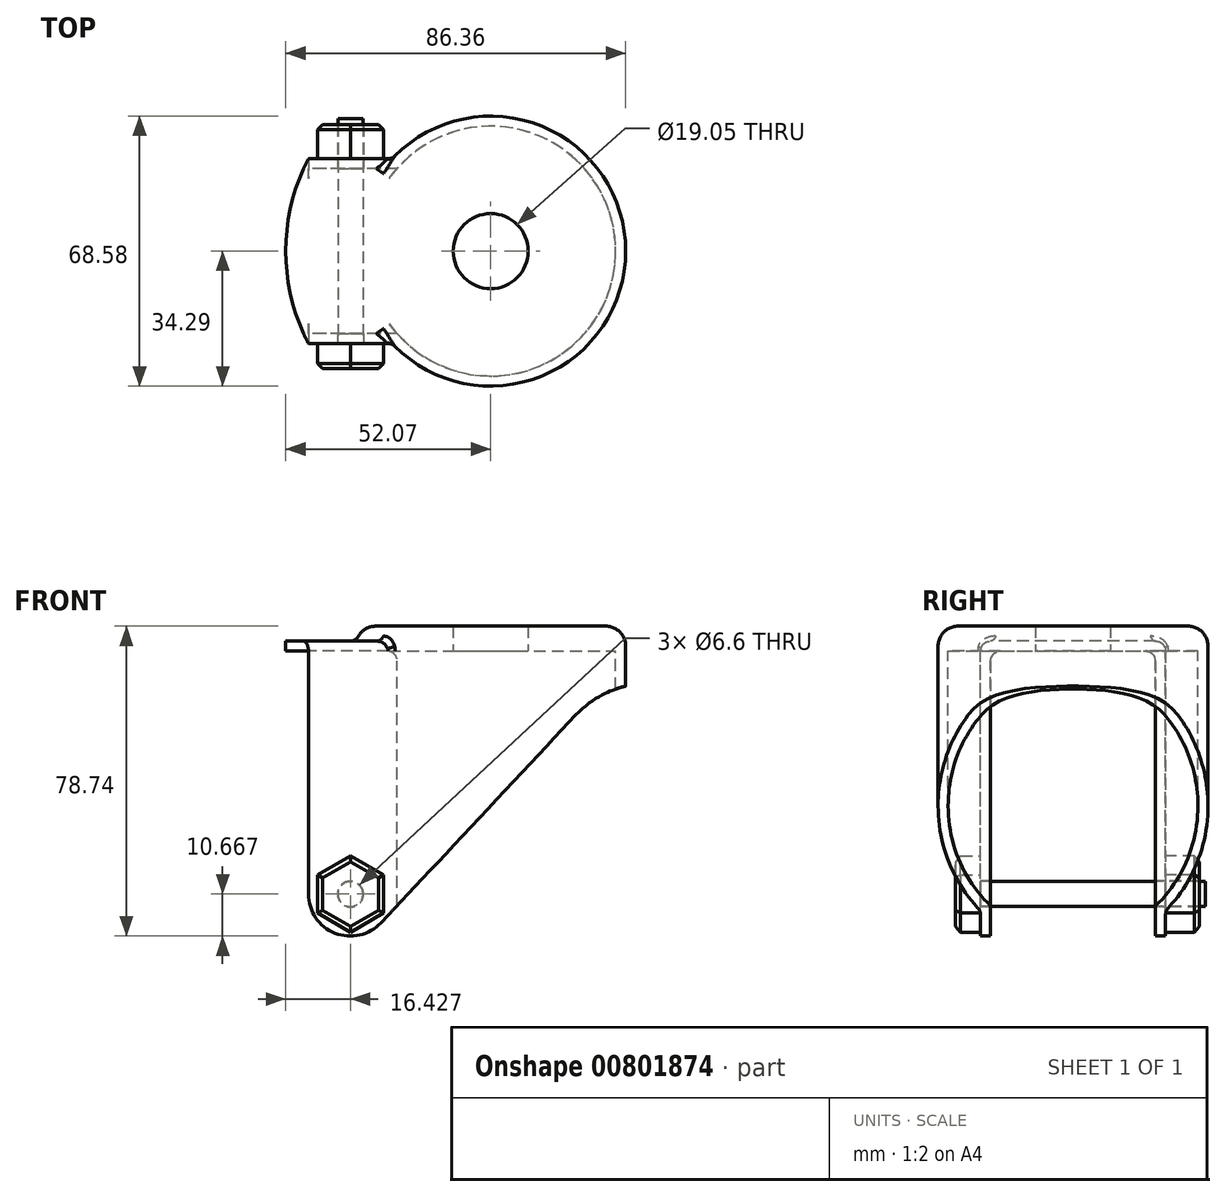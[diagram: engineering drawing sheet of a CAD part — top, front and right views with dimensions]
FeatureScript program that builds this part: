
annotation { "Feature Type Name" : "Feature", "Feature Type Description" : "" }
export const myFeature = defineFeature(function(context is Context, id is Id, definition is map)
    precondition{}
    {
        {
            var Q0;
            Q0=qCreatedBy(makeId("Top.planeOp"),FACE);
            var sketch = newSketch(context, id + "F0", { "sketchPlane" : qUnion([Q0])});
            skCircle(sketch, "E0", {"center": v(0, 0) * mm, "radius": 31.75 * mm});
            skLineSegment(sketch, "E1.bottom", {"start": v(0, 23.5) * mm, "end": v(-52.07, 23.5) * mm});
            skLineSegment(sketch, "E1.top", {"start": v(0, -23.5) * mm, "end": v(-52.07, -23.5) * mm});
            skLineSegment(sketch, "E1.left", {"start": v(0, 23.5) * mm, "end": v(0, -23.5) * mm});
            skLineSegment(sketch, "E1.right", {"start": v(-52.07, 23.5) * mm, "end": v(-52.07, -23.5) * mm});
            skPoint(sketch, "E1.middle", {"position": v(-26.04, 0) * mm});
            skLineSegment(sketch, "E2.0", {"start": v(0, -20.96) * mm, "end": v(-49.53, -20.96) * mm});
            skLineSegment(sketch, "E2.1", {"start": v(-49.53, 20.96) * mm, "end": v(-49.53, -20.96) * mm});
            skLineSegment(sketch, "E2.2", {"start": v(0, 20.95) * mm, "end": v(-49.53, 20.95) * mm});
            skCircle(sketch, "E3.0", {"center": v(0, 0) * mm, "radius": 34.3 * mm});
            skLineSegment(sketch, "E4", {"start": v(-49.53, 20.95) * mm, "end": v(-52.07, 20.95) * mm});
            skLineSegment(sketch, "E5", {"start": v(-49.53, -20.96) * mm, "end": v(-52.07, -20.96) * mm});
            skArc(sketch, "E6", {"start": v(-46.31, 23.5) * mm, "mid": v(-52.07, 0) * mm, "end": v(-46.31, -23.5) * mm});
            skLineSegment(sketch, "E7", {"start": v(-52.07, 0) * mm, "end": v(-31.75, 0) * mm, "construction": true});
            skArc(sketch, "E8", {"start": v(-44.74, 20.95) * mm, "mid": v(-49.53, 0) * mm, "end": v(-44.74, -20.96) * mm});
            skLineSegment(sketch, "E9", {"start": v(-46.31, 23.5) * mm, "end": v(-46.31, -23.5) * mm, "construction": true});
            skSolve(sketch);
        }
        {
            var Q0;
            {var subQ0=sQuery(id+"F0.wireOp",EDGE,"E2.0");var subQ1=sQuery(id+"F0.wireOp",EDGE,"E0");var subQ2=makeQuery(id+"F0.imprint","INTERSECT",VERTEX,{"derivedFrom":[subQ1,subQ0]});Q0=makeQuery(id+"F0.imprint","IMPRINT",FACE,{"disambiguationData":[TD([[makeQuery(id+"F0.imprint","IMPRINT",EDGE,{"disambiguationData":[TD([[subQ2,-1.0]])],"derivedFrom":subQ1}),-1.0]])]});}
            var Q1;
            {var subQ0=sQuery(id+"F0.wireOp",EDGE,"E2.2");var subQ1=sQuery(id+"F0.wireOp",EDGE,"E0");var subQ2=makeQuery(id+"F0.imprint","INTERSECT",VERTEX,{"derivedFrom":[subQ1,subQ0]});Q1=makeQuery(id+"F0.imprint","IMPRINT",FACE,{"disambiguationData":[TD([[makeQuery(id+"F0.imprint","IMPRINT",EDGE,{"disambiguationData":[TD([[subQ2,1.0]])],"derivedFrom":subQ1}),-1.0]])]});}
            var Q2;
            {var subQ0=sQuery(id+"F0.wireOp",EDGE,"E6");var subQ1=sQuery(id+"F0.wireOp",EDGE,"E2.1");var subQ2=makeQuery(id+"F0.imprint","INTERSECT",VERTEX,{"disambiguationData":[OD(0.0)],"derivedFrom":[subQ1,subQ0]});Q2=makeQuery(id+"F0.imprint","IMPRINT",FACE,{"disambiguationData":[TD([[makeQuery(id+"F0.imprint","IMPRINT",EDGE,{"disambiguationData":[TD([[subQ2,-1.0]])],"derivedFrom":subQ1}),-1.0]])]});}
            var Q3;
            {var subQ0=sQuery(id+"F0.wireOp",EDGE,"E1.bottom");var subQ1=sQuery(id+"F0.wireOp",EDGE,"E0");var subQ2=makeQuery(id+"F0.imprint","INTERSECT",VERTEX,{"derivedFrom":[subQ1,subQ0]});Q3=makeQuery(id+"F0.imprint","IMPRINT",FACE,{"disambiguationData":[TD([[makeQuery(id+"F0.imprint","IMPRINT",EDGE,{"disambiguationData":[TD([[subQ2,1.0]])],"derivedFrom":subQ1}),-1.0]])]});}
            var Q4;
            {var subQ0=sQuery(id+"F0.wireOp",EDGE,"E6");var subQ1=sQuery(id+"F0.wireOp",EDGE,"E2.1");var subQ2=makeQuery(id+"F0.imprint","INTERSECT",VERTEX,{"disambiguationData":[OD(0.0)],"derivedFrom":[subQ1,subQ0]});Q4=makeQuery(id+"F0.imprint","IMPRINT",FACE,{"disambiguationData":[TD([[makeQuery(id+"F0.imprint","IMPRINT",EDGE,{"disambiguationData":[TD([[subQ2,-1.0]])],"derivedFrom":subQ1}),1.0]])]});}
            var Q5;
            {var subQ1=sQuery(id+"F0.wireOp",EDGE,"E1.bottom");var subQ6=sQuery(id+"F0.wireOp",EDGE,"E6");var subQ8=makeQuery(id+"F0.imprint","INTERSECT",VERTEX,{"derivedFrom":[subQ1,subQ6]});Q5=makeQuery(id+"F0.imprint","IMPRINT",FACE,{"disambiguationData":[TD([[makeQuery(id+"F0.imprint","IMPRINT",EDGE,{"disambiguationData":[TD([[subQ8,1.0]])],"derivedFrom":subQ1}),1.0]])]});}
            var Q6;
            {var subQ0=sQuery(id+"F0.wireOp",EDGE,"E8");var subQ1=sQuery(id+"F0.wireOp",EDGE,"E2.0");var subQ2=makeQuery(id+"F0.imprint","INTERSECT",VERTEX,{"derivedFrom":[subQ1,subQ0]});Q6=makeQuery(id+"F0.imprint","IMPRINT",FACE,{"disambiguationData":[TD([[makeQuery(id+"F0.imprint","IMPRINT",EDGE,{"disambiguationData":[TD([[subQ2,-1.0]])],"derivedFrom":subQ1}),-1.0]])]});}
            var Q7;
            {var subQ2=sQuery(id+"F0.wireOp",EDGE,"E6");var subQ4=sQuery(id+"F0.wireOp",EDGE,"E1.top");var subQ5=makeQuery(id+"F0.imprint","INTERSECT",VERTEX,{"derivedFrom":[subQ4,subQ2]});Q7=makeQuery(id+"F0.imprint","IMPRINT",FACE,{"disambiguationData":[TD([[makeQuery(id+"F0.imprint","IMPRINT",EDGE,{"disambiguationData":[TD([[subQ5,1.0]])],"derivedFrom":subQ4}),-1.0]])]});}
            var Q8;
            {var subQ1=sQuery(id+"F0.wireOp",EDGE,"E2.0");var subQ5=sQuery(id+"F0.wireOp",EDGE,"E8");var subQ8=makeQuery(id+"F0.imprint","INTERSECT",VERTEX,{"derivedFrom":[subQ1,subQ5]});Q8=makeQuery(id+"F0.imprint","IMPRINT",FACE,{"disambiguationData":[TD([[makeQuery(id+"F0.imprint","IMPRINT",EDGE,{"disambiguationData":[TD([[subQ8,1.0]])],"derivedFrom":subQ1}),-1.0]])]});}
            var Q9;
            {var subQ0=sQuery(id+"F0.wireOp",EDGE,"E2.2");var subQ1=sQuery(id+"F0.wireOp",EDGE,"E0");var subQ2=makeQuery(id+"F0.imprint","INTERSECT",VERTEX,{"derivedFrom":[subQ1,subQ0]});Q9=makeQuery(id+"F0.imprint","IMPRINT",FACE,{"disambiguationData":[TD([[makeQuery(id+"F0.imprint","IMPRINT",EDGE,{"disambiguationData":[TD([[subQ2,-1.0]])],"derivedFrom":subQ1}),-1.0]])]});}
            var Q10;
            {var subQ0=sQuery(id+"F0.wireOp",EDGE,"E2.2");var subQ1=sQuery(id+"F0.wireOp",EDGE,"E0");var subQ2=makeQuery(id+"F0.imprint","INTERSECT",VERTEX,{"derivedFrom":[subQ1,subQ0]});Q10=makeQuery(id+"F0.imprint","IMPRINT",FACE,{"disambiguationData":[TD([[makeQuery(id+"F0.imprint","IMPRINT",EDGE,{"disambiguationData":[TD([[subQ2,-1.0]])],"derivedFrom":subQ1}),1.0]])]});}
            var Q11;
            {var subQ1=sQuery(id+"F0.wireOp",EDGE,"E1.bottom");var subQ4=sQuery(id+"F0.wireOp",EDGE,"E0");var subQ5=makeQuery(id+"F0.imprint","INTERSECT",VERTEX,{"derivedFrom":[subQ4,subQ1]});Q11=makeQuery(id+"F0.imprint","IMPRINT",FACE,{"disambiguationData":[TD([[makeQuery(id+"F0.imprint","IMPRINT",EDGE,{"disambiguationData":[TD([[subQ5,1.0]])],"derivedFrom":subQ4}),1.0]])]});}
            var Q12;
            {var subQ0=sQuery(id+"F0.wireOp",EDGE,"E2.2");var subQ1=sQuery(id+"F0.wireOp",EDGE,"E0");var subQ2=makeQuery(id+"F0.imprint","INTERSECT",VERTEX,{"derivedFrom":[subQ1,subQ0]});Q12=makeQuery(id+"F0.imprint","IMPRINT",FACE,{"disambiguationData":[TD([[makeQuery(id+"F0.imprint","IMPRINT",EDGE,{"disambiguationData":[TD([[subQ2,1.0]])],"derivedFrom":subQ1}),1.0]])]});}
            var Q13;
            {var subQ0=sQuery(id+"F0.wireOp",EDGE,"E2.0");var subQ1=sQuery(id+"F0.wireOp",EDGE,"E0");var subQ2=makeQuery(id+"F0.imprint","INTERSECT",VERTEX,{"derivedFrom":[subQ1,subQ0]});Q13=makeQuery(id+"F0.imprint","IMPRINT",FACE,{"disambiguationData":[TD([[makeQuery(id+"F0.imprint","IMPRINT",EDGE,{"disambiguationData":[TD([[subQ2,-1.0]])],"derivedFrom":subQ1}),1.0]])]});}
            extrude(context, id + "F1", {"entities" : qUnion([Q0, Q1, Q2, Q3, Q4, Q5, Q6, Q7, Q8, Q9, Q10, Q11, Q12, Q13]), "oppositeDirection" : true, "depth" : 72.39 * mm, "offsetDistance" : 25.4 * mm});
        }
        {
            var Q0;
            {var subQ0=sQuery(id+"F0.wireOp",EDGE,"E2.2");var subQ1=sQuery(id+"F0.wireOp",EDGE,"E0");var subQ2=makeQuery(id+"F0.imprint","INTERSECT",VERTEX,{"derivedFrom":[subQ1,subQ0]});Q0=makeQuery(id+"F0.imprint","IMPRINT",FACE,{"disambiguationData":[TD([[makeQuery(id+"F0.imprint","IMPRINT",EDGE,{"disambiguationData":[TD([[subQ2,-1.0]])],"derivedFrom":subQ1}),-1.0]])]});}
            var Q1;
            {var subQ0=sQuery(id+"F0.wireOp",EDGE,"E2.2");var subQ1=sQuery(id+"F0.wireOp",EDGE,"E0");var subQ2=makeQuery(id+"F0.imprint","INTERSECT",VERTEX,{"derivedFrom":[subQ1,subQ0]});Q1=makeQuery(id+"F0.imprint","IMPRINT",FACE,{"disambiguationData":[TD([[makeQuery(id+"F0.imprint","IMPRINT",EDGE,{"disambiguationData":[TD([[subQ2,1.0]])],"derivedFrom":subQ1}),-1.0]])]});}
            var Q2;
            {var subQ0=sQuery(id+"F0.wireOp",EDGE,"E1.bottom");var subQ1=sQuery(id+"F0.wireOp",EDGE,"E0");var subQ2=makeQuery(id+"F0.imprint","INTERSECT",VERTEX,{"derivedFrom":[subQ1,subQ0]});Q2=makeQuery(id+"F0.imprint","IMPRINT",FACE,{"disambiguationData":[TD([[makeQuery(id+"F0.imprint","IMPRINT",EDGE,{"disambiguationData":[TD([[subQ2,1.0]])],"derivedFrom":subQ1}),-1.0]])]});}
            var Q3;
            {var subQ1=sQuery(id+"F0.wireOp",EDGE,"E1.bottom");var subQ4=sQuery(id+"F0.wireOp",EDGE,"E0");var subQ5=makeQuery(id+"F0.imprint","INTERSECT",VERTEX,{"derivedFrom":[subQ4,subQ1]});Q3=makeQuery(id+"F0.imprint","IMPRINT",FACE,{"disambiguationData":[TD([[makeQuery(id+"F0.imprint","IMPRINT",EDGE,{"disambiguationData":[TD([[subQ5,1.0]])],"derivedFrom":subQ4}),1.0]])]});}
            var Q4;
            {var subQ0=sQuery(id+"F0.wireOp",EDGE,"E2.2");var subQ1=sQuery(id+"F0.wireOp",EDGE,"E0");var subQ2=makeQuery(id+"F0.imprint","INTERSECT",VERTEX,{"derivedFrom":[subQ1,subQ0]});Q4=makeQuery(id+"F0.imprint","IMPRINT",FACE,{"disambiguationData":[TD([[makeQuery(id+"F0.imprint","IMPRINT",EDGE,{"disambiguationData":[TD([[subQ2,1.0]])],"derivedFrom":subQ1}),1.0]])]});}
            var Q5;
            {var subQ0=sQuery(id+"F0.wireOp",EDGE,"E2.0");var subQ1=sQuery(id+"F0.wireOp",EDGE,"E0");var subQ2=makeQuery(id+"F0.imprint","INTERSECT",VERTEX,{"derivedFrom":[subQ1,subQ0]});Q5=makeQuery(id+"F0.imprint","IMPRINT",FACE,{"disambiguationData":[TD([[makeQuery(id+"F0.imprint","IMPRINT",EDGE,{"disambiguationData":[TD([[subQ2,-1.0]])],"derivedFrom":subQ1}),-1.0]])]});}
            var Q6;
            {var subQ0=sQuery(id+"F0.wireOp",EDGE,"E2.2");var subQ1=sQuery(id+"F0.wireOp",EDGE,"E0");var subQ2=makeQuery(id+"F0.imprint","INTERSECT",VERTEX,{"derivedFrom":[subQ1,subQ0]});Q6=makeQuery(id+"F0.imprint","IMPRINT",FACE,{"disambiguationData":[TD([[makeQuery(id+"F0.imprint","IMPRINT",EDGE,{"disambiguationData":[TD([[subQ2,-1.0]])],"derivedFrom":subQ1}),1.0]])]});}
            var Q7;
            {var subQ0=sQuery(id+"F0.wireOp",EDGE,"E2.0");var subQ1=sQuery(id+"F0.wireOp",EDGE,"E0");var subQ2=makeQuery(id+"F0.imprint","INTERSECT",VERTEX,{"derivedFrom":[subQ1,subQ0]});Q7=makeQuery(id+"F0.imprint","IMPRINT",FACE,{"disambiguationData":[TD([[makeQuery(id+"F0.imprint","IMPRINT",EDGE,{"disambiguationData":[TD([[subQ2,-1.0]])],"derivedFrom":subQ1}),1.0]])]});}
            var Q8;
            {var subQ0=sQuery(id+"F0.wireOp",EDGE,"E6");var subQ1=sQuery(id+"F0.wireOp",EDGE,"E2.1");var subQ2=makeQuery(id+"F0.imprint","INTERSECT",VERTEX,{"disambiguationData":[OD(0.0)],"derivedFrom":[subQ1,subQ0]});Q8=makeQuery(id+"F0.imprint","IMPRINT",FACE,{"disambiguationData":[TD([[makeQuery(id+"F0.imprint","IMPRINT",EDGE,{"disambiguationData":[TD([[subQ2,-1.0]])],"derivedFrom":subQ1}),-1.0]])]});}
            var Q9;
            {var subQ0=sQuery(id+"F0.wireOp",EDGE,"E8");var subQ1=sQuery(id+"F0.wireOp",EDGE,"E2.0");var subQ2=makeQuery(id+"F0.imprint","INTERSECT",VERTEX,{"derivedFrom":[subQ1,subQ0]});Q9=makeQuery(id+"F0.imprint","IMPRINT",FACE,{"disambiguationData":[TD([[makeQuery(id+"F0.imprint","IMPRINT",EDGE,{"disambiguationData":[TD([[subQ2,-1.0]])],"derivedFrom":subQ1}),-1.0]])]});}
            var Q10;
            {var subQ0=sQuery(id+"F0.wireOp",EDGE,"E6");var subQ1=sQuery(id+"F0.wireOp",EDGE,"E2.1");var subQ2=makeQuery(id+"F0.imprint","INTERSECT",VERTEX,{"disambiguationData":[OD(0.0)],"derivedFrom":[subQ1,subQ0]});Q10=makeQuery(id+"F0.imprint","IMPRINT",FACE,{"disambiguationData":[TD([[makeQuery(id+"F0.imprint","IMPRINT",EDGE,{"disambiguationData":[TD([[subQ2,-1.0]])],"derivedFrom":subQ1}),1.0]])]});}
            var Q11;
            {var subQ1=sQuery(id+"F0.wireOp",EDGE,"E1.bottom");var subQ6=sQuery(id+"F0.wireOp",EDGE,"E6");var subQ8=makeQuery(id+"F0.imprint","INTERSECT",VERTEX,{"derivedFrom":[subQ1,subQ6]});Q11=makeQuery(id+"F0.imprint","IMPRINT",FACE,{"disambiguationData":[TD([[makeQuery(id+"F0.imprint","IMPRINT",EDGE,{"disambiguationData":[TD([[subQ8,1.0]])],"derivedFrom":subQ1}),1.0]])]});}
            var Q12;
            {var subQ1=sQuery(id+"F0.wireOp",EDGE,"E2.0");var subQ5=sQuery(id+"F0.wireOp",EDGE,"E8");var subQ8=makeQuery(id+"F0.imprint","INTERSECT",VERTEX,{"derivedFrom":[subQ1,subQ5]});Q12=makeQuery(id+"F0.imprint","IMPRINT",FACE,{"disambiguationData":[TD([[makeQuery(id+"F0.imprint","IMPRINT",EDGE,{"disambiguationData":[TD([[subQ8,1.0]])],"derivedFrom":subQ1}),-1.0]])]});}
            var Q13;
            {var subQ2=sQuery(id+"F0.wireOp",EDGE,"E6");var subQ4=sQuery(id+"F0.wireOp",EDGE,"E1.top");var subQ5=makeQuery(id+"F0.imprint","INTERSECT",VERTEX,{"derivedFrom":[subQ4,subQ2]});Q13=makeQuery(id+"F0.imprint","IMPRINT",FACE,{"disambiguationData":[TD([[makeQuery(id+"F0.imprint","IMPRINT",EDGE,{"disambiguationData":[TD([[subQ5,1.0]])],"derivedFrom":subQ4}),-1.0]])]});}
            extrude(context, id + "F2", {"entities" : qUnion([Q0, Q1, Q2, Q3, Q4, Q5, Q6, Q7, Q8, Q9, Q10, Q11, Q12, Q13]), "operationType" : NewBodyOperationType.ADD, "depth" : 2.54 * mm, "offsetDistance" : 25.4 * mm});
        }
        {
            var Q0;
            Q0=qCreatedBy(makeId("Front.planeOp"),FACE);
            var sketch = newSketch(context, id + "F3", { "sketchPlane" : qUnion([Q0])});
            skCircle(sketch, "E10", {"center": v(-35.64, -61.72) * mm, "radius": 10.67 * mm});
            skLineSegment(sketch, "E11", {"start": v(21.59, -16.24) * mm, "end": v(-27.86, -69.02) * mm});
            skLineSegment(sketch, "E12", {"start": v(34.3, 2.54) * mm, "end": v(34.3, -8.9) * mm});
            skLineSegment(sketch, "E13", {"start": v(34.3, -8.9) * mm, "end": v(47, -8.9) * mm});
            skLineSegment(sketch, "E14", {"start": v(47, -8.9) * mm, "end": v(47, -85.1) * mm});
            skLineSegment(sketch, "E15", {"start": v(47, -85.1) * mm, "end": v(-59.01, -85.1) * mm});
            skLineSegment(sketch, "E16", {"start": v(-59.01, -85.1) * mm, "end": v(-59.01, -61.72) * mm});
            skLineSegment(sketch, "E17", {"start": v(-59.01, -61.72) * mm, "end": v(-35.64, -61.72) * mm});
            skArc(sketch, "E18", {"start": v(21.59, -16.24) * mm, "mid": v(27.4, -11.63) * mm, "end": v(34.3, -8.9) * mm});
            skLineSegment(sketch, "E19", {"start": v(-46.31, 0) * mm, "end": v(-46.31, -85.1) * mm});
            skLineSegment(sketch, "E20", {"start": v(-59.01, 0) * mm, "end": v(-46.31, 0) * mm});
            skLineSegment(sketch, "E21", {"start": v(-59.01, 0) * mm, "end": v(-59.01, -61.72) * mm});
            skSolve(sketch);
        }
        {
            var Q0;
            {var subQ1=sQuery(id+"F3.wireOp",EDGE,"E11");Q0=makeQuery(id+"F3.imprint","IMPRINT",FACE,{"disambiguationData":[TD([[makeQuery(id+"F3.imprint","IMPRINT",EDGE,{"derivedFrom":subQ1}),1.0]])]});}
            var Q1;
            {var subQ0=sQuery(id+"F3.wireOp",EDGE,"E16");Q1=makeQuery(id+"F3.imprint","IMPRINT",FACE,{"disambiguationData":[TD([[makeQuery(id+"F3.imprint","IMPRINT",EDGE,{"derivedFrom":subQ0}),-1.0]])]});}
            var Q2;
            {var subQ4=sQuery(id+"F3.wireOp",EDGE,"E20");Q2=makeQuery(id+"F3.imprint","IMPRINT",FACE,{"disambiguationData":[TD([[makeQuery(id+"F3.imprint","IMPRINT",EDGE,{"derivedFrom":subQ4}),-1.0]])]});}
            extrude(context, id + "F4", {"entities" : qUnion([Q0, Q1, Q2]), "operationType" : NewBodyOperationType.REMOVE, "endBound" : BoundingType.THROUGH_ALL, "oppositeDirection" : true, "depth" : 25.4 * mm, "offsetDistance" : 25.4 * mm, "hasSecondDirection" : true, "secondDirectionBound" : SecondDirectionBoundingType.THROUGH_ALL, "secondDirectionOppositeDirection" : false, "secondDirectionDepth" : 25.4 * mm});
        }
        {
            var Q0;
            {var subQ0=sQuery(id+"F0.wireOp",EDGE,"E1.bottom");var subQ1=sQuery(id+"F0.wireOp",EDGE,"E0");var subQ2=makeQuery(id+"F0.imprint","INTERSECT",VERTEX,{"derivedFrom":[subQ1,subQ0]});Q0=makeQuery(id+"F0.imprint","IMPRINT",FACE,{"disambiguationData":[TD([[makeQuery(id+"F0.imprint","IMPRINT",EDGE,{"disambiguationData":[TD([[subQ2,1.0]])],"derivedFrom":subQ1}),-1.0]])]});}
            var Q1;
            {var subQ0=sQuery(id+"F0.wireOp",EDGE,"E2.0");var subQ1=sQuery(id+"F0.wireOp",EDGE,"E0");var subQ2=makeQuery(id+"F0.imprint","INTERSECT",VERTEX,{"derivedFrom":[subQ1,subQ0]});Q1=makeQuery(id+"F0.imprint","IMPRINT",FACE,{"disambiguationData":[TD([[makeQuery(id+"F0.imprint","IMPRINT",EDGE,{"disambiguationData":[TD([[subQ2,-1.0]])],"derivedFrom":subQ1}),-1.0]])]});}
            var Q2;
            {var subQ0=sQuery(id+"F0.wireOp",EDGE,"E2.2");var subQ1=sQuery(id+"F0.wireOp",EDGE,"E0");var subQ2=makeQuery(id+"F0.imprint","INTERSECT",VERTEX,{"derivedFrom":[subQ1,subQ0]});Q2=makeQuery(id+"F0.imprint","IMPRINT",FACE,{"disambiguationData":[TD([[makeQuery(id+"F0.imprint","IMPRINT",EDGE,{"disambiguationData":[TD([[subQ2,-1.0]])],"derivedFrom":subQ1}),-1.0]])]});}
            var Q3;
            {var subQ0=sQuery(id+"F0.wireOp",EDGE,"E2.2");var subQ1=sQuery(id+"F0.wireOp",EDGE,"E0");var subQ2=makeQuery(id+"F0.imprint","INTERSECT",VERTEX,{"derivedFrom":[subQ1,subQ0]});Q3=makeQuery(id+"F0.imprint","IMPRINT",FACE,{"disambiguationData":[TD([[makeQuery(id+"F0.imprint","IMPRINT",EDGE,{"disambiguationData":[TD([[subQ2,1.0]])],"derivedFrom":subQ1}),-1.0]])]});}
            var Q4;
            {var subQ0=sQuery(id+"F0.wireOp",EDGE,"E2.2");var subQ1=sQuery(id+"F0.wireOp",EDGE,"E0");var subQ2=makeQuery(id+"F0.imprint","INTERSECT",VERTEX,{"derivedFrom":[subQ1,subQ0]});Q4=makeQuery(id+"F0.imprint","IMPRINT",FACE,{"disambiguationData":[TD([[makeQuery(id+"F0.imprint","IMPRINT",EDGE,{"disambiguationData":[TD([[subQ2,1.0]])],"derivedFrom":subQ1}),1.0]])]});}
            var Q5;
            {var subQ0=sQuery(id+"F0.wireOp",EDGE,"E2.2");var subQ1=sQuery(id+"F0.wireOp",EDGE,"E0");var subQ2=makeQuery(id+"F0.imprint","INTERSECT",VERTEX,{"derivedFrom":[subQ1,subQ0]});Q5=makeQuery(id+"F0.imprint","IMPRINT",FACE,{"disambiguationData":[TD([[makeQuery(id+"F0.imprint","IMPRINT",EDGE,{"disambiguationData":[TD([[subQ2,-1.0]])],"derivedFrom":subQ1}),1.0]])]});}
            var Q6;
            {var subQ1=sQuery(id+"F0.wireOp",EDGE,"E1.bottom");var subQ6=sQuery(id+"F0.wireOp",EDGE,"E0");var subQ8=makeQuery(id+"F0.imprint","INTERSECT",VERTEX,{"derivedFrom":[subQ6,subQ1]});Q6=makeQuery(id+"F0.imprint","IMPRINT",FACE,{"disambiguationData":[TD([[makeQuery(id+"F0.imprint","IMPRINT",EDGE,{"disambiguationData":[TD([[subQ8,1.0]])],"derivedFrom":subQ6}),1.0]])]});}
            var Q7;
            {var subQ0=sQuery(id+"F0.wireOp",EDGE,"E2.0");var subQ1=sQuery(id+"F0.wireOp",EDGE,"E0");var subQ2=makeQuery(id+"F0.imprint","INTERSECT",VERTEX,{"derivedFrom":[subQ1,subQ0]});Q7=makeQuery(id+"F0.imprint","IMPRINT",FACE,{"disambiguationData":[TD([[makeQuery(id+"F0.imprint","IMPRINT",EDGE,{"disambiguationData":[TD([[subQ2,-1.0]])],"derivedFrom":subQ1}),1.0]])]});}
            extrude(context, id + "F5", {"entities" : qUnion([Q0, Q1, Q2, Q3, Q4, Q5, Q6, Q7]), "operationType" : NewBodyOperationType.ADD, "depth" : 6.35 * mm, "offsetDistance" : 25.4 * mm});
        }
        {
            var Q0;
            {var subQ1=sQuery(id+"F0.wireOp",EDGE,"E1.bottom");var subQ4=sQuery(id+"F0.wireOp",EDGE,"E0");var subQ5=makeQuery(id+"F0.imprint","INTERSECT",VERTEX,{"derivedFrom":[subQ4,subQ1]});Q0=makeQuery(id+"F0.imprint","IMPRINT",FACE,{"disambiguationData":[TD([[makeQuery(id+"F0.imprint","IMPRINT",EDGE,{"disambiguationData":[TD([[subQ5,1.0]])],"derivedFrom":subQ4}),1.0]])]});}
            var Q1;
            {var subQ0=sQuery(id+"F0.wireOp",EDGE,"E2.0");var subQ1=sQuery(id+"F0.wireOp",EDGE,"E0");var subQ2=makeQuery(id+"F0.imprint","INTERSECT",VERTEX,{"derivedFrom":[subQ1,subQ0]});Q1=makeQuery(id+"F0.imprint","IMPRINT",FACE,{"disambiguationData":[TD([[makeQuery(id+"F0.imprint","IMPRINT",EDGE,{"disambiguationData":[TD([[subQ2,-1.0]])],"derivedFrom":subQ1}),1.0]])]});}
            var Q2;
            {var subQ0=sQuery(id+"F0.wireOp",EDGE,"E2.2");var subQ1=sQuery(id+"F0.wireOp",EDGE,"E0");var subQ2=makeQuery(id+"F0.imprint","INTERSECT",VERTEX,{"derivedFrom":[subQ1,subQ0]});Q2=makeQuery(id+"F0.imprint","IMPRINT",FACE,{"disambiguationData":[TD([[makeQuery(id+"F0.imprint","IMPRINT",EDGE,{"disambiguationData":[TD([[subQ2,-1.0]])],"derivedFrom":subQ1}),1.0]])]});}
            var Q3;
            {var subQ0=sQuery(id+"F0.wireOp",EDGE,"E2.2");var subQ1=sQuery(id+"F0.wireOp",EDGE,"E0");var subQ2=makeQuery(id+"F0.imprint","INTERSECT",VERTEX,{"derivedFrom":[subQ1,subQ0]});Q3=makeQuery(id+"F0.imprint","IMPRINT",FACE,{"disambiguationData":[TD([[makeQuery(id+"F0.imprint","IMPRINT",EDGE,{"disambiguationData":[TD([[subQ2,1.0]])],"derivedFrom":subQ1}),1.0]])]});}
            var Q4;
            {var subQ0=sQuery(id+"F0.wireOp",EDGE,"E2.2");var subQ1=sQuery(id+"F0.wireOp",EDGE,"E0");var subQ2=makeQuery(id+"F0.imprint","INTERSECT",VERTEX,{"derivedFrom":[subQ1,subQ0]});Q4=makeQuery(id+"F0.imprint","IMPRINT",FACE,{"disambiguationData":[TD([[makeQuery(id+"F0.imprint","IMPRINT",EDGE,{"disambiguationData":[TD([[subQ2,-1.0]])],"derivedFrom":subQ1}),-1.0]])]});}
            var Q5;
            {var subQ1=sQuery(id+"F0.wireOp",EDGE,"E2.0");var subQ5=sQuery(id+"F0.wireOp",EDGE,"E8");var subQ8=makeQuery(id+"F0.imprint","INTERSECT",VERTEX,{"derivedFrom":[subQ1,subQ5]});Q5=makeQuery(id+"F0.imprint","IMPRINT",FACE,{"disambiguationData":[TD([[makeQuery(id+"F0.imprint","IMPRINT",EDGE,{"disambiguationData":[TD([[subQ8,1.0]])],"derivedFrom":subQ1}),-1.0]])]});}
            var Q6;
            {var subQ0=sQuery(id+"F0.wireOp",EDGE,"E6");var subQ1=sQuery(id+"F0.wireOp",EDGE,"E2.1");var subQ2=makeQuery(id+"F0.imprint","INTERSECT",VERTEX,{"disambiguationData":[OD(0.0)],"derivedFrom":[subQ1,subQ0]});Q6=makeQuery(id+"F0.imprint","IMPRINT",FACE,{"disambiguationData":[TD([[makeQuery(id+"F0.imprint","IMPRINT",EDGE,{"disambiguationData":[TD([[subQ2,-1.0]])],"derivedFrom":subQ1}),1.0]])]});}
            var Q7;
            {var subQ0=sQuery(id+"F0.wireOp",EDGE,"E6");var subQ1=sQuery(id+"F0.wireOp",EDGE,"E2.1");var subQ2=makeQuery(id+"F0.imprint","INTERSECT",VERTEX,{"disambiguationData":[OD(0.0)],"derivedFrom":[subQ1,subQ0]});Q7=makeQuery(id+"F0.imprint","IMPRINT",FACE,{"disambiguationData":[TD([[makeQuery(id+"F0.imprint","IMPRINT",EDGE,{"disambiguationData":[TD([[subQ2,-1.0]])],"derivedFrom":subQ1}),-1.0]])]});}
            var Q8;
            {var subQ0=sQuery(id+"F0.wireOp",EDGE,"E8");var subQ1=sQuery(id+"F0.wireOp",EDGE,"E2.0");var subQ2=makeQuery(id+"F0.imprint","INTERSECT",VERTEX,{"derivedFrom":[subQ1,subQ0]});Q8=makeQuery(id+"F0.imprint","IMPRINT",FACE,{"disambiguationData":[TD([[makeQuery(id+"F0.imprint","IMPRINT",EDGE,{"disambiguationData":[TD([[subQ2,-1.0]])],"derivedFrom":subQ1}),-1.0]])]});}
            extrude(context, id + "F6", {"entities" : qUnion([Q0, Q1, Q2, Q3, Q4, Q5, Q6, Q7, Q8]), "operationType" : NewBodyOperationType.REMOVE, "endBound" : BoundingType.THROUGH_ALL, "oppositeDirection" : true, "depth" : 25.4 * mm, "offsetDistance" : 25.4 * mm});
        }
        {
            var Q0;
            Q0=qCreatedBy(makeId("Front.planeOp"),FACE);
            var sketch = newSketch(context, id + "F7", { "sketchPlane" : qUnion([Q0])});
            skCircle(sketch, "E22", {"center": v(-35.64, -61.72) * mm, "radius": 3.3 * mm});
            skSolve(sketch);
        }
        {
            var Q0;
            Q0=makeQuery(id+"F7.imprint","IMPRINT",FACE,{"disambiguationData":[TD([[makeQuery(id+"F7.imprint","IMPRINT",EDGE,{"derivedFrom":sQuery(id+"F7.wireOp",EDGE,"E22")}),1.0]])]});
            extrude(context, id + "F8", {"entities" : qUnion([Q0]), "operationType" : NewBodyOperationType.REMOVE, "endBound" : BoundingType.THROUGH_ALL, "oppositeDirection" : true, "depth" : 25.4 * mm, "offsetDistance" : 25.4 * mm, "hasSecondDirection" : true, "secondDirectionBound" : SecondDirectionBoundingType.THROUGH_ALL, "secondDirectionOppositeDirection" : false, "secondDirectionDepth" : 25.4 * mm});
        }
        {
            var Q0;
            Q0=makeQuery(id+"F5.opExtrude","CAP_EDGE",EDGE,{"disambiguationData":[OSD([sQuery(id+"F0.wireOp",EDGE,"E3.0")])],"isStart":false});
            fillet(context, id + "F9", {"entities" : qUnion([Q0]), "radius" : 5.08 * mm, "tangentPropagation" : true, "allowEdgeOverflow" : false});
        }
        {
            var Q0;
            Q0=makeQuery(id+"F2.opExtrude","CAP_EDGE",EDGE,{"disambiguationData":[OSD([sQuery(id+"F0.wireOp",EDGE,"E1.bottom")])],"isStart":false});
            var Q1;
            Q1=makeQuery(id+"F6.boolean.opBoolean","COPY",EDGE,{"derivedFrom":makeQuery(id+"F6.opExtrude","CAP_EDGE",EDGE,{"disambiguationData":[OSD([sQuery(id+"F0.wireOp",EDGE,"E2.2")])],"isStart":true})});
            var Q2;
            Q2=makeQuery(id+"F2.opExtrude","CAP_EDGE",EDGE,{"disambiguationData":[OSD([sQuery(id+"F0.wireOp",EDGE,"E1.top")])],"isStart":false});
            var Q3;
            Q3=makeQuery(id+"F6.boolean.opBoolean","COPY",EDGE,{"derivedFrom":makeQuery(id+"F6.opExtrude","CAP_EDGE",EDGE,{"disambiguationData":[OSD([sQuery(id+"F0.wireOp",EDGE,"E2.0")])],"isStart":true})});
            fillet(context, id + "F10", {"entities" : qUnion([Q0, Q1, Q2, Q3]), "radius" : 2.54 * mm, "tangentPropagation" : true, "allowEdgeOverflow" : false});
        }
        {
            var Q0;
            {var subQ0=sQuery(id+"F0.wireOp",EDGE,"E3.0");var subQ1=sQuery(id+"F0.wireOp",EDGE,"E1.bottom");Q0=makeQuery(id+"F2.boolean.opBoolean","MERGE",EDGE,{"derivedFrom":[makeQuery(id+"F1.opExtrude","SWEPT_EDGE",EDGE,{"disambiguationData":[OSD([subQ1,subQ0])]}),makeQuery(id+"F2.opExtrude","SWEPT_EDGE",EDGE,{"disambiguationData":[OSD([subQ1,subQ0])]})]});}
            fillet(context, id + "F11", {"entities" : qUnion([Q0]), "radius" : 2.54 * mm, "tangentPropagation" : true, "allowEdgeOverflow" : false});
        }
        {
            var Q0;
            Q0=qCreatedBy(makeId("Top.planeOp"),FACE);
            var sketch = newSketch(context, id + "F12", { "sketchPlane" : qUnion([Q0])});
            skCircle(sketch, "E23", {"center": v(0, 0) * mm, "radius": 9.53 * mm});
            skSolve(sketch);
        }
        {
            var Q0;
            Q0=makeQuery(id+"F12.imprint","IMPRINT",FACE,{"disambiguationData":[TD([[makeQuery(id+"F12.imprint","IMPRINT",EDGE,{"derivedFrom":sQuery(id+"F12.wireOp",EDGE,"E23")}),1.0]])]});
            extrude(context, id + "F13", {"entities" : qUnion([Q0]), "operationType" : NewBodyOperationType.REMOVE, "endBound" : BoundingType.THROUGH_ALL, "depth" : 25.4 * mm, "offsetDistance" : 25.4 * mm, "hasSecondDirection" : true, "secondDirectionBound" : SecondDirectionBoundingType.THROUGH_ALL, "secondDirectionOppositeDirection" : true, "secondDirectionDepth" : 25.4 * mm});
        }
        {
            var Q0;
            {var subQ0=sQuery(id+"F0.wireOp",EDGE,"E1.top");Q0=makeQuery(id+"F2.boolean.opBoolean","MERGE",FACE,{"derivedFrom":[makeQuery(id+"F1.opExtrude","SWEPT_FACE",FACE,{"disambiguationData":[OSD([subQ0])]}),makeQuery(id+"F2.opExtrude","SWEPT_FACE",FACE,{"disambiguationData":[OSD([subQ0])]})]});}
            var sketch = newSketch(context, id + "F14", { "sketchPlane" : qUnion([Q0])});
            skCircle(sketch, "E24.cCircle", {"center": v(-35.64, -61.72) * mm, "radius": 8.38 * mm, "construction": true});
            skLineSegment(sketch, "E24.0", {"start": v(-44.03, -56.88) * mm, "end": v(-35.64, -52.04) * mm});
            skLineSegment(sketch, "E24.1", {"start": v(-35.64, -52.04) * mm, "end": v(-27.26, -56.88) * mm});
            skLineSegment(sketch, "E24.2", {"start": v(-27.26, -56.88) * mm, "end": v(-27.26, -66.56) * mm});
            skLineSegment(sketch, "E24.3", {"start": v(-27.26, -66.56) * mm, "end": v(-35.64, -71.4) * mm});
            skLineSegment(sketch, "E24.4", {"start": v(-35.64, -71.4) * mm, "end": v(-44.03, -66.56) * mm});
            skLineSegment(sketch, "E24.5", {"start": v(-44.03, -66.56) * mm, "end": v(-44.03, -56.88) * mm});
            skPoint(sketch, "E24.0.midPoint", {"position": v(-39.83, -54.46) * mm});
            skCircle(sketch, "E25", {"center": v(-35.64, -61.72) * mm, "radius": 3.17 * mm});
            skSolve(sketch);
        }
        {
            var Q0;
            Q0=makeQuery(id+"F14.imprint","IMPRINT",FACE,{"disambiguationData":[TD([[makeQuery(id+"F14.imprint","IMPRINT",EDGE,{"derivedFrom":sQuery(id+"F14.wireOp",EDGE,"E24.0")}),-1.0]])]});
            var Q1;
            Q1=makeQuery(id+"F14.imprint","IMPRINT",FACE,{"disambiguationData":[TD([[makeQuery(id+"F14.imprint","IMPRINT",EDGE,{"derivedFrom":sQuery(id+"F14.wireOp",EDGE,"E25")}),1.0]])]});
            var Q2;
            Q2=makeQuery(id+"F14.imprint","IMPRINT",FACE,{"disambiguationData":[TD([[makeQuery(id+"F14.imprint","IMPRINT",EDGE,{"derivedFrom":sQuery(id+"F14.wireOp",EDGE,"E25")}),-1.0]])]});
            extrude(context, id + "F15", {"entities" : qUnion([Q0, Q1, Q2]), "depth" : 6.35 * mm, "offsetDistance" : 25.4 * mm});
        }
        {
            var Q0;
            Q0=makeQuery(id+"F14.imprint","IMPRINT",FACE,{"disambiguationData":[TD([[makeQuery(id+"F14.imprint","IMPRINT",EDGE,{"derivedFrom":sQuery(id+"F14.wireOp",EDGE,"E25")}),1.0]])]});
            extrude(context, id + "F16", {"entities" : qUnion([Q0]), "operationType" : NewBodyOperationType.ADD, "oppositeDirection" : true, "depth" : 57.15 * mm, "offsetDistance" : 25.4 * mm});
        }
        {
            var Q0;
            {var subQ0=sQuery(id+"F0.wireOp",EDGE,"E1.bottom");Q0=makeQuery(id+"F2.boolean.opBoolean","MERGE",FACE,{"derivedFrom":[makeQuery(id+"F1.opExtrude","SWEPT_FACE",FACE,{"disambiguationData":[OSD([subQ0])]}),makeQuery(id+"F2.opExtrude","SWEPT_FACE",FACE,{"disambiguationData":[OSD([subQ0])]})]});}
            var sketch = newSketch(context, id + "F17", { "sketchPlane" : qUnion([Q0])});
            skCircle(sketch, "E26.cCircle", {"center": v(35.64, -61.72) * mm, "radius": 8.38 * mm, "construction": true});
            skLineSegment(sketch, "E26.0", {"start": v(27.26, -56.88) * mm, "end": v(35.64, -52.04) * mm});
            skLineSegment(sketch, "E26.1", {"start": v(35.64, -52.04) * mm, "end": v(44.03, -56.88) * mm});
            skLineSegment(sketch, "E26.2", {"start": v(44.03, -56.88) * mm, "end": v(44.03, -66.56) * mm});
            skLineSegment(sketch, "E26.3", {"start": v(44.03, -66.56) * mm, "end": v(35.64, -71.4) * mm});
            skLineSegment(sketch, "E26.4", {"start": v(35.64, -71.4) * mm, "end": v(27.26, -66.56) * mm});
            skLineSegment(sketch, "E26.5", {"start": v(27.26, -66.56) * mm, "end": v(27.26, -56.88) * mm});
            skPoint(sketch, "E26.0.midPoint", {"position": v(31.45, -54.46) * mm});
            skCircle(sketch, "E27", {"center": v(35.64, -61.72) * mm, "radius": 3.3 * mm});
            skSolve(sketch);
        }
        {
            var Q0;
            Q0=makeQuery(id+"F17.imprint","IMPRINT",FACE,{"disambiguationData":[TD([[makeQuery(id+"F17.imprint","IMPRINT",EDGE,{"derivedFrom":sQuery(id+"F17.wireOp",EDGE,"E26.0")}),-1.0]])]});
            extrude(context, id + "F18", {"entities" : qUnion([Q0]), "depth" : 8.64 * mm, "offsetDistance" : 25.4 * mm});
        }
        {
            var Q0;
            Q0=makeQuery(id+"F15.opExtrude","CAP_EDGE",EDGE,{"disambiguationData":[OSD([sQuery(id+"F14.wireOp",EDGE,"E24.1")])],"isStart":false});
            var Q1;
            Q1=makeQuery(id+"F15.opExtrude","CAP_EDGE",EDGE,{"disambiguationData":[OSD([sQuery(id+"F14.wireOp",EDGE,"E24.0")])],"isStart":false});
            var Q2;
            Q2=makeQuery(id+"F15.opExtrude","CAP_EDGE",EDGE,{"disambiguationData":[OSD([sQuery(id+"F14.wireOp",EDGE,"E24.5")])],"isStart":false});
            var Q3;
            Q3=makeQuery(id+"F15.opExtrude","CAP_EDGE",EDGE,{"disambiguationData":[OSD([sQuery(id+"F14.wireOp",EDGE,"E24.4")])],"isStart":false});
            var Q4;
            Q4=makeQuery(id+"F15.opExtrude","CAP_EDGE",EDGE,{"disambiguationData":[OSD([sQuery(id+"F14.wireOp",EDGE,"E24.3")])],"isStart":false});
            var Q5;
            Q5=makeQuery(id+"F15.opExtrude","CAP_EDGE",EDGE,{"disambiguationData":[OSD([sQuery(id+"F14.wireOp",EDGE,"E24.2")])],"isStart":false});
            var Q6;
            Q6=makeQuery(id+"F18.opExtrude","CAP_EDGE",EDGE,{"disambiguationData":[OSD([sQuery(id+"F17.wireOp",EDGE,"E26.2")])],"isStart":false});
            var Q7;
            Q7=makeQuery(id+"F18.opExtrude","CAP_EDGE",EDGE,{"disambiguationData":[OSD([sQuery(id+"F17.wireOp",EDGE,"E26.1")])],"isStart":false});
            var Q8;
            Q8=makeQuery(id+"F18.opExtrude","CAP_EDGE",EDGE,{"disambiguationData":[OSD([sQuery(id+"F17.wireOp",EDGE,"E26.0")])],"isStart":false});
            var Q9;
            Q9=makeQuery(id+"F18.opExtrude","CAP_EDGE",EDGE,{"disambiguationData":[OSD([sQuery(id+"F17.wireOp",EDGE,"E26.5")])],"isStart":false});
            var Q10;
            Q10=makeQuery(id+"F18.opExtrude","CAP_EDGE",EDGE,{"disambiguationData":[OSD([sQuery(id+"F17.wireOp",EDGE,"E26.4")])],"isStart":false});
            var Q11;
            Q11=makeQuery(id+"F18.opExtrude","CAP_EDGE",EDGE,{"disambiguationData":[OSD([sQuery(id+"F17.wireOp",EDGE,"E26.3")])],"isStart":false});
            chamfer(context, id + "F19", {"entities" : qUnion([Q0, Q1, Q2, Q3, Q4, Q5, Q6, Q7, Q8, Q9, Q10, Q11]), "width" : 1.27 * mm, "tangentPropagation" : true});
        }
    });
